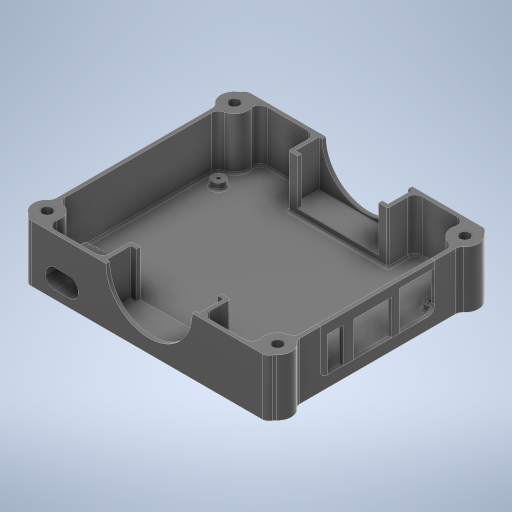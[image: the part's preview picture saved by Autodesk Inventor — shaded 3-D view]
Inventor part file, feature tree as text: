
AUTODESK INVENTOR PART (.ipt)
format: ipt  version: 2023.3 (Build 273359000, 359)  size: 1,134,080 bytes
history: native  units: in
note: dims shown in document units (in); Inventor stores cm internally (conversion verified against a paired STEP export)
features: sketch x20, extrude x18, reference x11, projected_geometry x11, other x4, plane x3, fillet x3, hole x2
ambient origin geometry x8: Origin, YZ Plane, XZ Plane, XY Plane, X Axis, Y Axis, Z Axis, Center Point
bodies: Solid1 (feature_tree), Solid2 (feature_tree), Solid3 (feature_tree), Solid4 (feature_tree)
feature tree (72):
  plane  "Work Plane1"
  extrude  "Extrusion1"  Depth=0.04in
  extrude  "Extrusion2"  Depth=0.5512in
  extrude  "Extrusion3"  Depth=0.065in
  extrude  "Extrusion4"  TaperAngle=0.0deg  [1 undecoded]
  extrude  "Extrusion5"  Depth=0.7874in TaperAngle=0.0deg
  extrude  "Extrusion6"  Depth=0.0787in TaperAngle=0.0deg
  sketch  "Sketch7"  dims[d16=0.05in d17=0.1181in d18=0.0in]
  plane  "Work Plane2"
  extrude  "Extrusion7"  Depth=0.1181in TaperAngle=0.0deg
  extrude  "Extrusion8"  Depth=0.1181in TaperAngle=0.0deg
  extrude  "Extrusion9"  Depth=0.1181in TaperAngle=0.0deg
  sketch  "Sketch10"  dims[d28=1.7853in d29=0.05in]
  plane  "Work Plane3"
  extrude  "Extrusion10"  Depth=0.05in
  extrude  "Extrusion11"  Depth=0.05in
  extrude  "Extrusion12"  Depth=0.8661in
  hole  "Hole1"  [1 undecoded]
  extrude  "Extrusion13"  Depth=0.1in
  fillet  "Fillet1"  Radius=0.1in
  extrude  "Extrusion14"  Depth=0.063in
  fillet  "Fillet2"  Radius=0.063in
  hole  "Hole2"  [1 undecoded]
  fillet  "Fillet3"  Radius=1.0in
  extrude  "Extrusion15"  Depth=1.7323in
  extrude  "Extrusion16"  Depth=1.0in TaperAngle=0.0deg
  extrude  "Extrusion17"  Depth=0.1in
  extrude  "Extrusion18"  Depth=0.063in
  sketch  "Sketch1"  dims[d0=0.04in d1=0.04in]
  reference  "Reference1"
  reference  "Reference2"
  sketch  "Sketch2"  dims[d2=0.5512in d3=0.5512in]
  projected_geometry  "Projected Loop1"
  sketch  "Sketch3"  dims[d5=0.065in d6=0.065in]
  sketch  "Sketch4"  dims[d7=0.065in d8=0.0in]
  reference  "Reference3"
  reference  "Reference4"
  reference  "Reference5"
  reference  "Reference6"
  sketch  "Sketch5"  dims[d9=0.065in d10=0.7874in d11=0.0in]
  reference  "Reference7"
  reference  "Reference8"
  reference  "Reference9"
  sketch  "Sketch6"  dims[d12=0.1969in d13=0.0in d14=0.0787in d15=0.0in]
  reference  "Reference10"
  reference  "Reference11"
  sketch  "Sketch8"  dims[d19=0.6378in d22=0.1181in d23=0.0in]
  projected_geometry  "Projected Loop2"
  sketch  "Sketch9"  dims[d24=0.05in d25=0.1181in d26=0.0in]
  sketch  "Sketch11"  dims[d30=0.15in d31=0.05in]
  sketch  "Sketch12"  dims[d32=1.7323in d33=0.8661in]
  sketch  "Sketch13"  dims[d34=0.4843in d35=1.0in d36=0.0in]
  sketch  "Sketch14"  dims[d45=1.0in d46=0.0in d47=0.1in d48=0.1in]
  projected_geometry  "Projected Loop3"
  projected_geometry  "Projected Loop4"
  sketch  "Sketch15"  dims[d49=0.063in d50=0.063in d51=0.063in]
  sketch  "Sketch17"  dims[d52=0.063in d53=1.4961in d54=1.0in d55=0.0in]
  sketch  "Sketch18"  dims[d56=0.4724in d57=1.7323in]
  projected_geometry  "Projected Loop5"
  sketch  "Sketch19"  dims[d58=0.8661in d59=1.0in d60=0.0in]
  projected_geometry  "Projected Loop6"
  sketch  "Sketch20"  dims[d62=0.063in d63=0.1in]
  projected_geometry  "Projected Loop7"
  projected_geometry  "Projected Loop8"
  projected_geometry  "Projected Loop9"
  projected_geometry  "Projected Loop10"
  sketch  "Sketch21"  dims[d64=0.063in d65=0.063in d66=0.063in d67=0.1in d68=1.0in d69=0.0in d70=1.4961in d71=1.0in d72=0.0in d73=0.0617in d74=0.157in d75=0.173in d76=0.079in d77=0.5635in d78=1.0in d79=0.8108in d80=0.0394in d81=0.625in d82=0.0in d83=0.125in d84=3.25in d85=4.0in d86=0.4724in d87=0.1969in d88=0.0in d89=0.125in d90=0.177in d91=0.75in d92=0.313in d93=0.75in d94=0.5635in d95=1.0in d96=0.8108in d97=0.0312in d98=0.0079in d99=0.0in d100=0.0079in d101=0.0in d102=0.0079in d103=0.0in d104=0.0079in d105=0.0in]
  projected_geometry  "Projected Loop11"
  other  "OrangePICover.iam"
  other  "OPi5_pcb_asm-0809:1"
  other  "orangepicover-002:1"
  other  "Assembly10"
note: 3 required parameter values undecoded (feature->parameter linkage not recoverable at this tier; creation-order binding heuristic only, values carry confidence <= 0.55)
